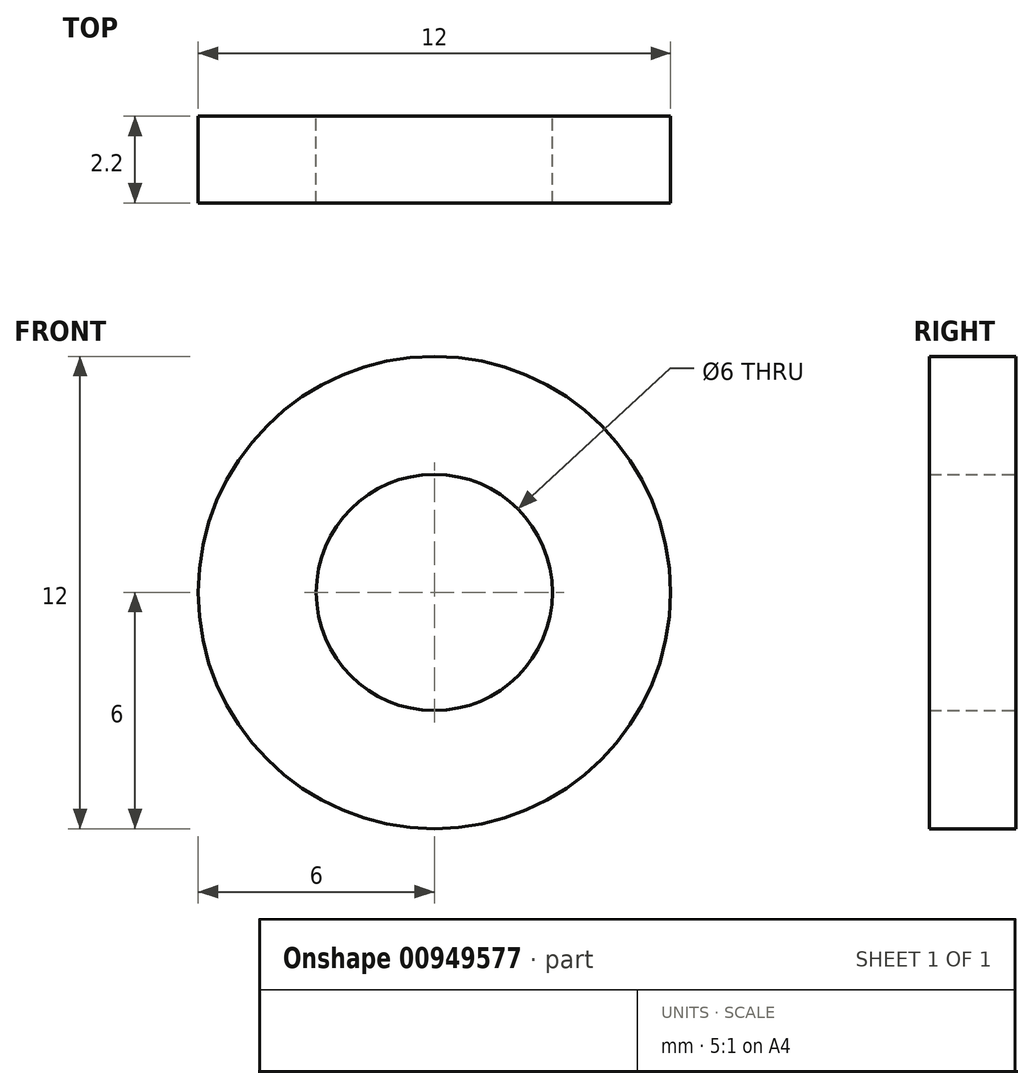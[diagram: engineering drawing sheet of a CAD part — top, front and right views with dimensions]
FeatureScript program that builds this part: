
annotation { "Feature Type Name" : "Feature", "Feature Type Description" : "" }
export const myFeature = defineFeature(function(context is Context, id is Id, definition is map)
    precondition{}
    {
        {
            var Q0;
            Q0=qCreatedBy(makeId("Front.planeOp"),FACE);
            var sketch = newSketch(context, id + "F0", { "sketchPlane" : qUnion([Q0])});
            skCircle(sketch, "E0", {"center": v(0, 0) * mm, "radius": 6 * mm});
            skCircle(sketch, "E1", {"center": v(0, 0) * mm, "radius": 3 * mm});
            skSolve(sketch);
        }
        {
            var Q0;
            Q0 = qSketchRegion(id + "F0", true);
            extrude(context, id + "F1", {"entities" : qUnion([Q0]), "depth" : 2.2 * mm, "offsetDistance" : 25 * mm});
        }
    });
